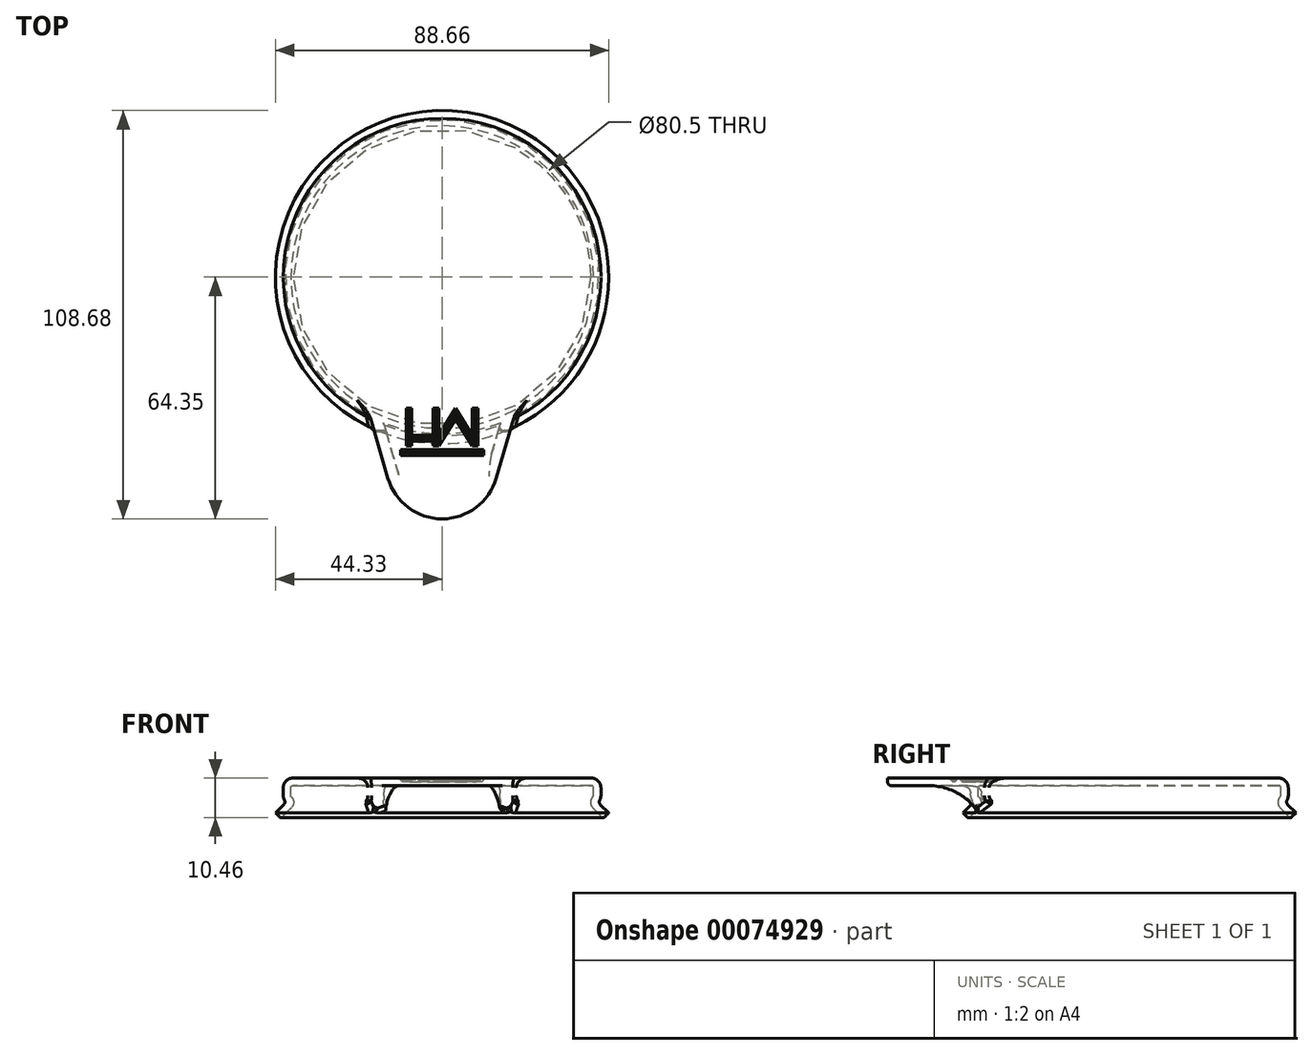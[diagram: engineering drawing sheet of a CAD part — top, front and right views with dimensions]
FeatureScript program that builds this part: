
annotation { "Feature Type Name" : "Feature", "Feature Type Description" : "" }
export const myFeature = defineFeature(function(context is Context, id is Id, definition is map)
    precondition{}
    {
        {
            var Q0;
            Q0=qCreatedBy(makeId("Front.planeOp"),FACE);
            var sketch = newSketch(context, id + "F0", { "sketchPlane" : qUnion([Q0])});
            skLineSegment(sketch, "E0", {"start": v(0, 0) * mm, "end": v(-39.75, 0) * mm});
            skArc(sketch, "E1", {"start": v(-40.1, -3) * mm, "mid": v(-39.5, -4.42) * mm, "end": v(-40.09, -5.84) * mm});
            skLineSegment(sketch, "E2", {"start": v(-40.09, -5.84) * mm, "end": v(-42.91, -8.67) * mm});
            skLineSegment(sketch, "E3.3", {"start": v(0, 2) * mm, "end": v(-39.75, 2) * mm});
            skLineSegment(sketch, "E4", {"start": v(-39.75, 0) * mm, "end": v(-39.75, -2.66) * mm, "construction": true});
            skLineSegment(sketch, "E5", {"start": v(-40.25, -0.74) * mm, "end": v(-40.25, -1.66) * mm, "construction": true});
            skArc(sketch, "E6", {"start": v(-39.75, 0) * mm, "mid": v(-40.1, -0.15) * mm, "end": v(-40.25, -0.5) * mm});
            skLineSegment(sketch, "E7", {"start": v(-40.25, -0.5) * mm, "end": v(-40.25, -2.64) * mm});
            skArc(sketch, "E8", {"start": v(-40.25, -2.64) * mm, "mid": v(-40.21, -2.84) * mm, "end": v(-40.1, -3) * mm});
            skLineSegment(sketch, "E9.bottom", {"start": v(-38.5, 0) * mm, "end": v(-40.25, 0) * mm, "construction": true});
            skLineSegment(sketch, "E9.top", {"start": v(-38.5, -3) * mm, "end": v(-40.25, -3) * mm, "construction": true});
            skLineSegment(sketch, "E9.left", {"start": v(-38.5, 0) * mm, "end": v(-38.5, -3) * mm, "construction": true});
            skLineSegment(sketch, "E9.right", {"start": v(-40.25, 0) * mm, "end": v(-40.25, -3) * mm, "construction": true});
            skLineSegment(sketch, "E10", {"start": v(-39.5, -2.72) * mm, "end": v(-39.5, -3.84) * mm, "construction": true});
            skLineSegment(sketch, "E11.0", {"start": v(-42.25, -0.5) * mm, "end": v(-42.25, -2.64) * mm});
            skArc(sketch, "E11.1", {"start": v(-39.75, 2) * mm, "mid": v(-41.52, 1.27) * mm, "end": v(-42.25, -0.5) * mm});
            skArc(sketch, "E12.0", {"start": v(-42.25, -2.64) * mm, "mid": v(-42.05, -3.61) * mm, "end": v(-41.5, -4.43) * mm});
            skLineSegment(sketch, "E13", {"start": v(-41.5, -4.43) * mm, "end": v(-44.33, -7.26) * mm});
            skLineSegment(sketch, "E14", {"start": v(-44.33, -7.26) * mm, "end": v(-42.91, -8.67) * mm});
            skLineSegment(sketch, "E15", {"start": v(0, 2) * mm, "end": v(0, 0) * mm});
            skSolve(sketch);
        }
        {
            var Q0;
            Q0=makeQuery(id+"F0.imprint","IMPRINT",FACE,{"disambiguationData":[TD([[makeQuery(id+"F0.imprint","IMPRINT",EDGE,{"derivedFrom":sQuery(id+"F0.wireOp",EDGE,"E0")}),-1.0]])]});
            var Q1;
            Q1=sQuery(id+"F0.wireOp",EDGE,"E15");
            revolve(context, id + "F1", {"entities" : qUnion([Q0]), "axis" : qUnion([Q1]), "revolveType" : RevolveType.FULL});
        }
        {
            var Q0;
            Q0=makeQuery(id+"F1.opRevolve","SWEPT_EDGE",EDGE,{"disambiguationData":[OSD([sQuery(id+"F0.wireOp",EDGE,"E12.0"),sQuery(id+"F0.wireOp",EDGE,"E13")])]});
            fillet(context, id + "F2", {"entities" : qUnion([Q0]), "radius" : 1 * mm, "tangentPropagation" : true, "allowEdgeOverflow" : false});
        }
        {
            var Q0;
            Q0=makeQuery(id+"F1.opRevolve","SWEPT_FACE",FACE,{"disambiguationData":[OSD([sQuery(id+"F0.wireOp",EDGE,"E3.3")])]});
            var sketch = newSketch(context, id + "F3", { "sketchPlane" : qUnion([Q0])});
            skLineSegment(sketch, "E16", {"start": v(0, 0) * mm, "end": v(0, -64.35) * mm, "construction": true});
            skArc(sketch, "E17", {"start": v(0, -64.35) * mm, "mid": v(9, -61.35) * mm, "end": v(14.4, -53.55) * mm});
            skLineSegment(sketch, "E18", {"start": v(14.4, -53.55) * mm, "end": v(20, -34.35) * mm});
            skLineSegment(sketch, "E19", {"start": v(20, -34.35) * mm, "end": v(0, -34.35) * mm});
            skArc(sketch, "E20.MirrorCS", {"start": v(0, -64.35) * mm, "mid": v(-9, -61.35) * mm, "end": v(-14.4, -53.55) * mm});
            skLineSegment(sketch, "E21.MirrorCS", {"start": v(-20, -34.35) * mm, "end": v(0, -34.35) * mm});
            skLineSegment(sketch, "E22.MirrorCS", {"start": v(-14.4, -53.55) * mm, "end": v(-20, -34.35) * mm});
            skSolve(sketch);
        }
        {
            var Q0;
            Q0=makeQuery(id+"F3.imprint","IMPRINT",FACE,{"disambiguationData":[TD([[makeQuery(id+"F3.imprint","IMPRINT",EDGE,{"derivedFrom":sQuery(id+"F3.wireOp",EDGE,"E17")}),1.0]])]});
            var Q1;
            {var subQ0=sQuery(id+"F3.wireOp",EDGE,"E19");Q1=makeQuery(id+"F3.imprint","IMPRINT",FACE,{"disambiguationData":[TD([[makeQuery(id+"F3.imprint","IMPRINT",EDGE,{"derivedFrom":subQ0}),1.0]])]});}
            extrude(context, id + "F4", {"entities" : qUnion([Q0, Q1]), "operationType" : NewBodyOperationType.ADD, "oppositeDirection" : true, "depth" : 2 * mm});
        }
        {
            var Q0;
            Q0=makeQuery(id+"F4.opExtrude","SWEPT_FACE",FACE,{"disambiguationData":[OSD([sQuery(id+"F3.wireOp",EDGE,"E18")])]});
            var sketch = newSketch(context, id + "F5", { "sketchPlane" : qUnion([Q0])});
            skArc(sketch, "E23", {"start": v(-30.83, 0) * mm, "mid": v(-30.87, -0.25) * mm, "end": v(-30.9, -0.5) * mm});
            skLineSegment(sketch, "E24", {"start": v(-30.9, -0.5) * mm, "end": v(-30.9, -2.64) * mm});
            skArc(sketch, "E25", {"start": v(-30.9, -2.64) * mm, "mid": v(-30.76, -3.27) * mm, "end": v(-30.47, -3.85) * mm});
            skArc(sketch, "E26", {"start": v(-30.7, -5.04) * mm, "mid": v(-30.39, -4.48) * mm, "end": v(-30.47, -3.85) * mm});
            skLineSegment(sketch, "E27", {"start": v(-30.7, -5.04) * mm, "end": v(-33.68, -7.26) * mm});
            skLineSegment(sketch, "E28", {"start": v(-30.83, 0) * mm, "end": v(-47.38, 0) * mm});
            skLineSegment(sketch, "E29", {"start": v(-47.38, 0) * mm, "end": v(-33.68, -7.26) * mm, "construction": true});
            skArc(sketch, "E30", {"start": v(-33.68, -7.26) * mm, "mid": v(-39.63, -1.93) * mm, "end": v(-47.38, 0) * mm});
            skSolve(sketch);
        }
        {
            var Q0;
            Q0=makeQuery(id+"F5.imprint","IMPRINT",FACE,{"disambiguationData":[TD([[makeQuery(id+"F5.imprint","IMPRINT",EDGE,{"derivedFrom":sQuery(id+"F5.wireOp",EDGE,"E23")}),-1.0]])]});
            extrude(context, id + "F6", {"entities" : qUnion([Q0]), "oppositeDirection" : true, "depth" : 3 * mm});
        }
        {
            var Q0;
            Q0=makeQuery(id+"F6.opExtrude","SWEPT_BODY",BODY,{"disambiguationData":[OSD([sQuery(id+"F5.wireOp",EDGE,"E23"),sQuery(id+"F5.wireOp",EDGE,"E24"),sQuery(id+"F5.wireOp",EDGE,"E25"),sQuery(id+"F5.wireOp",EDGE,"E26"),sQuery(id+"F5.wireOp",EDGE,"E27"),sQuery(id+"F5.wireOp",EDGE,"E28"),sQuery(id+"F5.wireOp",EDGE,"E30")])]});
            var Q1;
            Q1=qCreatedBy(makeId("Right.planeOp"),FACE);
            mirror(context, id + "F7", {"operationType" : NewBodyOperationType.ADD, "entities" : qUnion([Q0]), "mirrorPlane" : qUnion([Q1])});
        }
        {
            var Q0;
            Q0=makeQuery(id+"F4.boolean.opBoolean","INTERSECT",EDGE,{"derivedFrom":[makeQuery(id+"F1.opRevolve","SWEPT_FACE",FACE,{"disambiguationData":[OSD([sQuery(id+"F0.wireOp",EDGE,"E11.1")])]}),makeQuery(id+"F4.opExtrude","CAP_FACE",FACE,{"disambiguationData":[OSD([sQuery(id+"F3.wireOp",EDGE,"E17"),sQuery(id+"F3.wireOp",EDGE,"E18"),sQuery(id+"F3.wireOp",EDGE,"E19"),sQuery(id+"F3.wireOp",EDGE,"E20.MirrorCS"),sQuery(id+"F3.wireOp",EDGE,"E21.MirrorCS"),sQuery(id+"F3.wireOp",EDGE,"E22.MirrorCS")])],"isStart":false})]});
            fillet(context, id + "F8", {"entities" : qUnion([Q0]), "radius" : 10 * mm, "tangentPropagation" : true, "allowEdgeOverflow" : false});
        }
        {
            var Q0;
            {var subQ0=makeQuery(id+"F1.opRevolve","SWEPT_FACE",FACE,{"disambiguationData":[OSD([sQuery(id+"F0.wireOp",EDGE,"E11.1")])]});var subQ1=makeQuery(id+"F6.opExtrude","CAP_FACE",FACE,{"disambiguationData":[OSD([sQuery(id+"F5.wireOp",EDGE,"E23"),sQuery(id+"F5.wireOp",EDGE,"E24"),sQuery(id+"F5.wireOp",EDGE,"E25"),sQuery(id+"F5.wireOp",EDGE,"E26"),sQuery(id+"F5.wireOp",EDGE,"E27"),sQuery(id+"F5.wireOp",EDGE,"E28"),sQuery(id+"F5.wireOp",EDGE,"E30")])],"isStart":false});Q0=makeQuery(id+"F8.opFillet","BLEND_EDGE",EDGE,{"blendedFrom":[makeQuery(id+"F4.boolean.opBoolean","INTERSECT",EDGE,{"derivedFrom":[subQ0,makeQuery(id+"F4.opExtrude","CAP_FACE",FACE,{"disambiguationData":[OSD([sQuery(id+"F3.wireOp",EDGE,"E17"),sQuery(id+"F3.wireOp",EDGE,"E18"),sQuery(id+"F3.wireOp",EDGE,"E19"),sQuery(id+"F3.wireOp",EDGE,"E20.MirrorCS"),sQuery(id+"F3.wireOp",EDGE,"E21.MirrorCS"),sQuery(id+"F3.wireOp",EDGE,"E22.MirrorCS")])],"isStart":false})]}),makeQuery(id+"F7.boolean.opBoolean","SPLIT",FACE,{"disambiguationData":[TD([subQ1])],"derivedFrom":makeQuery(id+"F1.opRevolve","SWEPT_FACE",FACE,{"disambiguationData":[OSD([sQuery(id+"F0.wireOp",EDGE,"E11.0")])]})})],"blendedInto":[makeQuery(id+"F7.boolean.opBoolean","SPLIT",FACE,{"disambiguationData":[TD([subQ1])],"derivedFrom":makeQuery(id+"F1.opRevolve","SWEPT_FACE",FACE,{"disambiguationData":[OSD([sQuery(id+"F0.wireOp",EDGE,"E11.0")])]})})]});}
            fillet(context, id + "F9", {"entities" : qUnion([Q0]), "radius" : 2 * mm, "tangentPropagation" : true, "allowEdgeOverflow" : false});
        }
        {
            var Q0;
            Q0=makeQuery(id+"F6.opExtrude","CAP_EDGE",EDGE,{"disambiguationData":[OSD([sQuery(id+"F5.wireOp",EDGE,"E28")])],"isStart":false});
            var Q1;
            Q1=makeQuery(id+"F7.opPattern","COPY",EDGE,{"derivedFrom":makeQuery(id+"F6.opExtrude","CAP_EDGE",EDGE,{"disambiguationData":[OSD([sQuery(id+"F5.wireOp",EDGE,"E28")])],"isStart":false}),"instanceName":"1"});
            var Q2;
            Q2=makeQuery(id+"F7.boolean.opBoolean","INTERSECT",EDGE,{"derivedFrom":[makeQuery(id+"F1.opRevolve","SWEPT_FACE",FACE,{"disambiguationData":[OSD([sQuery(id+"F0.wireOp",EDGE,"E13")])]}),makeQuery(id+"F7.opPattern","COPY",FACE,{"derivedFrom":makeQuery(id+"F6.opExtrude","SWEPT_FACE",FACE,{"disambiguationData":[OSD([sQuery(id+"F5.wireOp",EDGE,"E30")])]}),"instanceName":"1"})]});
            var Q3;
            Q3=makeQuery(id+"F7.boolean.opBoolean","INTERSECT",EDGE,{"derivedFrom":[makeQuery(id+"F1.opRevolve","SWEPT_FACE",FACE,{"disambiguationData":[OSD([sQuery(id+"F0.wireOp",EDGE,"E13")])]}),makeQuery(id+"F6.opExtrude","SWEPT_FACE",FACE,{"disambiguationData":[OSD([sQuery(id+"F5.wireOp",EDGE,"E30")])]})]});
            fillet(context, id + "F10", {"entities" : qUnion([Q0, Q1, Q2, Q3]), "radius" : 1 * mm, "tangentPropagation" : true, "allowEdgeOverflow" : false});
        }
        {
            var Q0;
            Q0=makeQuery(id+"F7.boolean.opBoolean","INTERSECT",EDGE,{"derivedFrom":[makeQuery(id+"F1.opRevolve","SWEPT_FACE",FACE,{"disambiguationData":[OSD([sQuery(id+"F0.wireOp",EDGE,"E13")])]}),makeQuery(id+"F6.opExtrude","CAP_FACE",FACE,{"disambiguationData":[OSD([sQuery(id+"F5.wireOp",EDGE,"E23"),sQuery(id+"F5.wireOp",EDGE,"E24"),sQuery(id+"F5.wireOp",EDGE,"E25"),sQuery(id+"F5.wireOp",EDGE,"E26"),sQuery(id+"F5.wireOp",EDGE,"E27"),sQuery(id+"F5.wireOp",EDGE,"E28"),sQuery(id+"F5.wireOp",EDGE,"E30")])],"isStart":true})]});
            var Q1;
            Q1=makeQuery(id+"F6.opExtrude","CAP_EDGE",EDGE,{"disambiguationData":[OSD([sQuery(id+"F5.wireOp",EDGE,"E26")])],"isStart":true});
            var Q2;
            Q2=makeQuery(id+"F7.boolean.opBoolean","INTERSECT",EDGE,{"derivedFrom":[makeQuery(id+"F1.opRevolve","SWEPT_FACE",FACE,{"disambiguationData":[OSD([sQuery(id+"F0.wireOp",EDGE,"E12.0")])]}),makeQuery(id+"F6.opExtrude","CAP_FACE",FACE,{"disambiguationData":[OSD([sQuery(id+"F5.wireOp",EDGE,"E23"),sQuery(id+"F5.wireOp",EDGE,"E24"),sQuery(id+"F5.wireOp",EDGE,"E25"),sQuery(id+"F5.wireOp",EDGE,"E26"),sQuery(id+"F5.wireOp",EDGE,"E27"),sQuery(id+"F5.wireOp",EDGE,"E28"),sQuery(id+"F5.wireOp",EDGE,"E30")])],"isStart":true})]});
            var Q3;
            Q3=makeQuery(id+"F6.opExtrude","CAP_EDGE",EDGE,{"disambiguationData":[OSD([sQuery(id+"F5.wireOp",EDGE,"E24")])],"isStart":true});
            var Q4;
            Q4=makeQuery(id+"F4.boolean.opBoolean","INTERSECT",EDGE,{"derivedFrom":[makeQuery(id+"F1.opRevolve","SWEPT_FACE",FACE,{"disambiguationData":[OSD([sQuery(id+"F0.wireOp",EDGE,"E11.1")])]}),makeQuery(id+"F4.opExtrude","SWEPT_FACE",FACE,{"disambiguationData":[OSD([sQuery(id+"F3.wireOp",EDGE,"E18")])]})]});
            var Q5;
            Q5=makeQuery(id+"F7.boolean.opBoolean","INTERSECT",EDGE,{"derivedFrom":[makeQuery(id+"F1.opRevolve","SWEPT_FACE",FACE,{"disambiguationData":[OSD([sQuery(id+"F0.wireOp",EDGE,"E11.1")])]}),makeQuery(id+"F6.opExtrude","CAP_FACE",FACE,{"disambiguationData":[OSD([sQuery(id+"F5.wireOp",EDGE,"E23"),sQuery(id+"F5.wireOp",EDGE,"E24"),sQuery(id+"F5.wireOp",EDGE,"E25"),sQuery(id+"F5.wireOp",EDGE,"E26"),sQuery(id+"F5.wireOp",EDGE,"E27"),sQuery(id+"F5.wireOp",EDGE,"E28"),sQuery(id+"F5.wireOp",EDGE,"E30")])],"isStart":true})]});
            var Q6;
            Q6=makeQuery(id+"F4.boolean.opBoolean","INTERSECT",EDGE,{"derivedFrom":[makeQuery(id+"F1.opRevolve","SWEPT_FACE",FACE,{"disambiguationData":[OSD([sQuery(id+"F0.wireOp",EDGE,"E11.1")])]}),makeQuery(id+"F4.opExtrude","SWEPT_FACE",FACE,{"disambiguationData":[OSD([sQuery(id+"F3.wireOp",EDGE,"E22.MirrorCS")])]})]});
            var Q7;
            Q7=makeQuery(id+"F7.boolean.opBoolean","INTERSECT",EDGE,{"derivedFrom":[makeQuery(id+"F1.opRevolve","SWEPT_FACE",FACE,{"disambiguationData":[OSD([sQuery(id+"F0.wireOp",EDGE,"E11.1")])]}),makeQuery(id+"F7.opPattern","COPY",FACE,{"derivedFrom":makeQuery(id+"F6.opExtrude","CAP_FACE",FACE,{"disambiguationData":[OSD([sQuery(id+"F5.wireOp",EDGE,"E23"),sQuery(id+"F5.wireOp",EDGE,"E24"),sQuery(id+"F5.wireOp",EDGE,"E25"),sQuery(id+"F5.wireOp",EDGE,"E26"),sQuery(id+"F5.wireOp",EDGE,"E27"),sQuery(id+"F5.wireOp",EDGE,"E28"),sQuery(id+"F5.wireOp",EDGE,"E30")])],"isStart":true}),"instanceName":"1"})]});
            var Q8;
            Q8=makeQuery(id+"F7.opPattern","COPY",EDGE,{"derivedFrom":makeQuery(id+"F6.opExtrude","CAP_EDGE",EDGE,{"disambiguationData":[OSD([sQuery(id+"F5.wireOp",EDGE,"E26")])],"isStart":true}),"instanceName":"1"});
            var Q9;
            Q9=makeQuery(id+"F7.boolean.opBoolean","INTERSECT",EDGE,{"derivedFrom":[makeQuery(id+"F1.opRevolve","SWEPT_FACE",FACE,{"disambiguationData":[OSD([sQuery(id+"F0.wireOp",EDGE,"E13")])]}),makeQuery(id+"F7.opPattern","COPY",FACE,{"derivedFrom":makeQuery(id+"F6.opExtrude","CAP_FACE",FACE,{"disambiguationData":[OSD([sQuery(id+"F5.wireOp",EDGE,"E23"),sQuery(id+"F5.wireOp",EDGE,"E24"),sQuery(id+"F5.wireOp",EDGE,"E25"),sQuery(id+"F5.wireOp",EDGE,"E26"),sQuery(id+"F5.wireOp",EDGE,"E27"),sQuery(id+"F5.wireOp",EDGE,"E28"),sQuery(id+"F5.wireOp",EDGE,"E30")])],"isStart":true}),"instanceName":"1"})]});
            var Q10;
            Q10=makeQuery(id+"F7.boolean.opBoolean","INTERSECT",EDGE,{"derivedFrom":[makeQuery(id+"F1.opRevolve","SWEPT_FACE",FACE,{"disambiguationData":[OSD([sQuery(id+"F0.wireOp",EDGE,"E12.0")])]}),makeQuery(id+"F7.opPattern","COPY",FACE,{"derivedFrom":makeQuery(id+"F6.opExtrude","CAP_FACE",FACE,{"disambiguationData":[OSD([sQuery(id+"F5.wireOp",EDGE,"E23"),sQuery(id+"F5.wireOp",EDGE,"E24"),sQuery(id+"F5.wireOp",EDGE,"E25"),sQuery(id+"F5.wireOp",EDGE,"E26"),sQuery(id+"F5.wireOp",EDGE,"E27"),sQuery(id+"F5.wireOp",EDGE,"E28"),sQuery(id+"F5.wireOp",EDGE,"E30")])],"isStart":true}),"instanceName":"1"})]});
            var Q11;
            Q11=makeQuery(id+"F7.opPattern","COPY",EDGE,{"derivedFrom":makeQuery(id+"F6.opExtrude","CAP_EDGE",EDGE,{"disambiguationData":[OSD([sQuery(id+"F5.wireOp",EDGE,"E24")])],"isStart":true}),"instanceName":"1"});
            fillet(context, id + "F11", {"entities" : qUnion([Q0, Q1, Q2, Q3, Q4, Q5, Q6, Q7, Q8, Q9, Q10, Q11]), "radius" : 2 * mm, "tangentPropagation" : true, "allowEdgeOverflow" : false});
        }
        {
            var Q0;
            Q0=makeQuery(id+"F6.opExtrude","CAP_EDGE",EDGE,{"disambiguationData":[OSD([sQuery(id+"F5.wireOp",EDGE,"E30")])],"isStart":true});
            var Q1;
            Q1=makeQuery(id+"F10.opFillet","BLEND_EDGE",EDGE,{"blendedFrom":[makeQuery(id+"F7.opPattern","COPY",EDGE,{"derivedFrom":makeQuery(id+"F6.opExtrude","CAP_EDGE",EDGE,{"disambiguationData":[OSD([sQuery(id+"F5.wireOp",EDGE,"E28")])],"isStart":false}),"instanceName":"1"}),makeQuery(id+"F7.opPattern","COPY",FACE,{"derivedFrom":makeQuery(id+"F6.opExtrude","SWEPT_FACE",FACE,{"disambiguationData":[OSD([sQuery(id+"F5.wireOp",EDGE,"E30")])]}),"instanceName":"1"})],"blendedInto":[makeQuery(id+"F7.opPattern","COPY",FACE,{"derivedFrom":makeQuery(id+"F6.opExtrude","SWEPT_FACE",FACE,{"disambiguationData":[OSD([sQuery(id+"F5.wireOp",EDGE,"E30")])]}),"instanceName":"1"})]});
            var Q2;
            Q2=makeQuery(id+"F6.opExtrude","CAP_EDGE",EDGE,{"disambiguationData":[OSD([sQuery(id+"F5.wireOp",EDGE,"E30")])],"isStart":false});
            fillet(context, id + "F12", {"entities" : qUnion([Q0, Q1, Q2]), "radius" : 1 * mm, "tangentPropagation" : true, "allowEdgeOverflow" : false});
        }
        {
            var Q0;
            Q0=qCreatedBy(makeId("Right.planeOp"),FACE);
            var sketch = newSketch(context, id + "F13", { "sketchPlane" : qUnion([Q0])});
            skLineSegment(sketch, "E31", {"start": v(39.75, 0) * mm, "end": v(0, 0) * mm});
            skArc(sketch, "E32", {"start": v(40.25, -0.5) * mm, "mid": v(40.1, -0.15) * mm, "end": v(39.75, 0) * mm});
            skLineSegment(sketch, "E33", {"start": v(40.25, -2.64) * mm, "end": v(40.25, -0.5) * mm});
            skArc(sketch, "E34", {"start": v(40.1, -3) * mm, "mid": v(40.21, -2.84) * mm, "end": v(40.25, -2.64) * mm});
            skArc(sketch, "E35", {"start": v(40.09, -5.84) * mm, "mid": v(39.5, -4.42) * mm, "end": v(40.1, -3) * mm});
            skLineSegment(sketch, "E36", {"start": v(42.91, -8.67) * mm, "end": v(40.09, -5.84) * mm});
            skLineSegment(sketch, "E37", {"start": v(0, 0) * mm, "end": v(0, -8.67) * mm});
            skLineSegment(sketch, "E38", {"start": v(0, -8.67) * mm, "end": v(42.91, -8.67) * mm});
            skSolve(sketch);
        }
        {
            var Q0;
            Q0=makeQuery(id+"F13.imprint","IMPRINT",FACE,{"disambiguationData":[TD([[makeQuery(id+"F13.imprint","IMPRINT",EDGE,{"derivedFrom":sQuery(id+"F13.wireOp",EDGE,"E31")}),1.0]])]});
            var Q1;
            Q1=sQuery(id+"F13.wireOp",EDGE,"E37");
            revolve(context, id + "F14", {"operationType" : NewBodyOperationType.REMOVE, "entities" : qUnion([Q0]), "axis" : qUnion([Q1]), "revolveType" : RevolveType.FULL, "oppositeDirection" : true});
        }
        {
            var Q0;
            Q0=makeQuery(id+"F4.boolean.opBoolean","MERGE",FACE,{"derivedFrom":[makeQuery(id+"F1.opRevolve","SWEPT_FACE",FACE,{"disambiguationData":[OSD([sQuery(id+"F0.wireOp",EDGE,"E3.3")])]}),makeQuery(id+"F4.opExtrude","CAP_FACE",FACE,{"disambiguationData":[OSD([sQuery(id+"F3.wireOp",EDGE,"E17"),sQuery(id+"F3.wireOp",EDGE,"E18"),sQuery(id+"F3.wireOp",EDGE,"E19"),sQuery(id+"F3.wireOp",EDGE,"E20.MirrorCS"),sQuery(id+"F3.wireOp",EDGE,"E21.MirrorCS"),sQuery(id+"F3.wireOp",EDGE,"E22.MirrorCS")])],"isStart":true})]});
            var sketch = newSketch(context, id + "F15", { "sketchPlane" : qUnion([Q0])});
            skLineSegment(sketch, "E39", {"start": v(-9.55, -34.94) * mm, "end": v(-8.05, -34.94) * mm});
            skLineSegment(sketch, "E40", {"start": v(-8.05, -34.94) * mm, "end": v(-8.05, -42.1) * mm});
            skLineSegment(sketch, "E41", {"start": v(-8.05, -42.1) * mm, "end": v(-2.33, -42.1) * mm});
            skLineSegment(sketch, "E42", {"start": v(-2.33, -42.1) * mm, "end": v(-2.33, -34.94) * mm});
            skLineSegment(sketch, "E43", {"start": v(-2.33, -34.94) * mm, "end": v(-0.83, -34.94) * mm});
            skLineSegment(sketch, "E44", {"start": v(-0.83, -34.94) * mm, "end": v(-0.83, -42.1) * mm});
            skLineSegment(sketch, "E45", {"start": v(-0.83, -42.1) * mm, "end": v(3.61, -34.94) * mm});
            skLineSegment(sketch, "E46", {"start": v(3.61, -34.94) * mm, "end": v(8.05, -42.1) * mm});
            skLineSegment(sketch, "E47", {"start": v(8.05, -42.1) * mm, "end": v(8.05, -34.94) * mm});
            skLineSegment(sketch, "E48", {"start": v(8.05, -34.94) * mm, "end": v(9.55, -34.94) * mm});
            skLineSegment(sketch, "E49", {"start": v(9.55, -34.94) * mm, "end": v(9.55, -44.94) * mm});
            skLineSegment(sketch, "E50", {"start": v(9.55, -44.94) * mm, "end": v(8.05, -44.94) * mm});
            skLineSegment(sketch, "E51", {"start": v(8.05, -44.94) * mm, "end": v(3.61, -37.79) * mm});
            skLineSegment(sketch, "E52", {"start": v(3.61, -37.79) * mm, "end": v(-0.83, -44.94) * mm});
            skLineSegment(sketch, "E53", {"start": v(-0.83, -44.94) * mm, "end": v(-2.33, -44.94) * mm});
            skLineSegment(sketch, "E54", {"start": v(-2.33, -44.94) * mm, "end": v(-2.33, -43.6) * mm});
            skLineSegment(sketch, "E55", {"start": v(-2.33, -43.6) * mm, "end": v(-8.05, -43.6) * mm});
            skLineSegment(sketch, "E56", {"start": v(-8.05, -43.6) * mm, "end": v(-8.05, -44.94) * mm});
            skLineSegment(sketch, "E57", {"start": v(-8.05, -44.94) * mm, "end": v(-9.55, -44.94) * mm});
            skLineSegment(sketch, "E58", {"start": v(-9.55, -44.94) * mm, "end": v(-9.55, -34.94) * mm});
            skLineSegment(sketch, "E59", {"start": v(-8.05, -34.94) * mm, "end": v(8.05, -34.94) * mm, "construction": true});
            skLineSegment(sketch, "E60", {"start": v(-8.05, -44.94) * mm, "end": v(9.55, -44.94) * mm, "construction": true});
            skLineSegment(sketch, "E61", {"start": v(-2.33, -42.1) * mm, "end": v(-2.33, -43.6) * mm, "construction": true});
            skLineSegment(sketch, "E62", {"start": v(-8.05, -42.1) * mm, "end": v(-8.05, -43.6) * mm, "construction": true});
            skLineSegment(sketch, "E63", {"start": v(-0.83, -42.1) * mm, "end": v(-0.83, -44.94) * mm, "construction": true});
            skLineSegment(sketch, "E64", {"start": v(3.61, -34.94) * mm, "end": v(3.61, -37.79) * mm, "construction": true});
            skLineSegment(sketch, "E65", {"start": v(2.34, -37) * mm, "end": v(3.61, -37.79) * mm, "construction": true});
            skLineSegment(sketch, "E66", {"start": v(3.61, -37.79) * mm, "end": v(4.89, -37) * mm, "construction": true});
            skLineSegment(sketch, "E67", {"start": v(0, -64.35) * mm, "end": v(0, -44.94) * mm, "construction": true});
            skLineSegment(sketch, "E68", {"start": v(-9.55, -44.94) * mm, "end": v(9.55, -44.94) * mm, "construction": true});
            skLineSegment(sketch, "E69", {"start": v(-2.33, -42.1) * mm, "end": v(-0.83, -42.1) * mm, "construction": true});
            skLineSegment(sketch, "E70.rect.bottom", {"start": v(11.03, -45.94) * mm, "end": v(-11.03, -45.94) * mm});
            skLineSegment(sketch, "E70.rect.top", {"start": v(11.03, -47.44) * mm, "end": v(-11.03, -47.44) * mm});
            skLineSegment(sketch, "E70.rect.left", {"start": v(11.03, -45.94) * mm, "end": v(11.03, -47.44) * mm});
            skLineSegment(sketch, "E70.rect.right", {"start": v(-11.03, -45.94) * mm, "end": v(-11.03, -47.44) * mm});
            skPoint(sketch, "E70.rect.middle", {"position": v(0, -46.7) * mm});
            skSolve(sketch);
        }
        {
            var Q0;
            Q0=makeQuery(id+"F15.imprint","IMPRINT",FACE,{"disambiguationData":[TD([[makeQuery(id+"F15.imprint","IMPRINT",EDGE,{"derivedFrom":sQuery(id+"F15.wireOp",EDGE,"E39")}),-1.0]])]});
            var Q1;
            Q1=makeQuery(id+"F15.imprint","IMPRINT",FACE,{"disambiguationData":[TD([[makeQuery(id+"F15.imprint","IMPRINT",EDGE,{"derivedFrom":sQuery(id+"F15.wireOp",EDGE,"E70.rect.bottom")}),1.0]])]});
            extrude(context, id + "F16", {"entities" : qUnion([Q0, Q1]), "operationType" : NewBodyOperationType.REMOVE, "oppositeDirection" : true, "depth" : 1 * mm});
        }
        {
            var Q0;
            Q0=makeQuery(id+"F16.boolean.opBoolean","COPY",FACE,{"derivedFrom":makeQuery(id+"F16.opExtrude","CAP_FACE",FACE,{"disambiguationData":[OSD([sQuery(id+"F15.wireOp",EDGE,"E39"),sQuery(id+"F15.wireOp",EDGE,"E40"),sQuery(id+"F15.wireOp",EDGE,"E41"),sQuery(id+"F15.wireOp",EDGE,"E42"),sQuery(id+"F15.wireOp",EDGE,"E43"),sQuery(id+"F15.wireOp",EDGE,"E44"),sQuery(id+"F15.wireOp",EDGE,"E45"),sQuery(id+"F15.wireOp",EDGE,"E46"),sQuery(id+"F15.wireOp",EDGE,"E47"),sQuery(id+"F15.wireOp",EDGE,"E48"),sQuery(id+"F15.wireOp",EDGE,"E49"),sQuery(id+"F15.wireOp",EDGE,"E50"),sQuery(id+"F15.wireOp",EDGE,"E51"),sQuery(id+"F15.wireOp",EDGE,"E52"),sQuery(id+"F15.wireOp",EDGE,"E53"),sQuery(id+"F15.wireOp",EDGE,"E54"),sQuery(id+"F15.wireOp",EDGE,"E55"),sQuery(id+"F15.wireOp",EDGE,"E56"),sQuery(id+"F15.wireOp",EDGE,"E57"),sQuery(id+"F15.wireOp",EDGE,"E58")])],"isStart":false})});
            var Q1;
            Q1=makeQuery(id+"F16.boolean.opBoolean","COPY",FACE,{"derivedFrom":makeQuery(id+"F16.opExtrude","CAP_FACE",FACE,{"disambiguationData":[OSD([sQuery(id+"F15.wireOp",EDGE,"E70.rect.bottom"),sQuery(id+"F15.wireOp",EDGE,"E70.rect.top"),sQuery(id+"F15.wireOp",EDGE,"E70.rect.left"),sQuery(id+"F15.wireOp",EDGE,"E70.rect.right")])],"isStart":false})});
            chamfer(context, id + "F17", {"entities" : qUnion([Q0, Q1]), "width" : .5 * mm, "tangentPropagation" : true});
        }
        {
            var Q0;
            Q0=makeQuery(id+"F1.opRevolve","SWEPT_EDGE",EDGE,{"disambiguationData":[OSD([sQuery(id+"F0.wireOp",EDGE,"E2"),sQuery(id+"F0.wireOp",EDGE,"E14")])]});
            fillet(context, id + "F18", {"entities" : qUnion([Q0]), "radius" : .5 * mm, "tangentPropagation" : true, "allowEdgeOverflow" : false});
        }
    });
